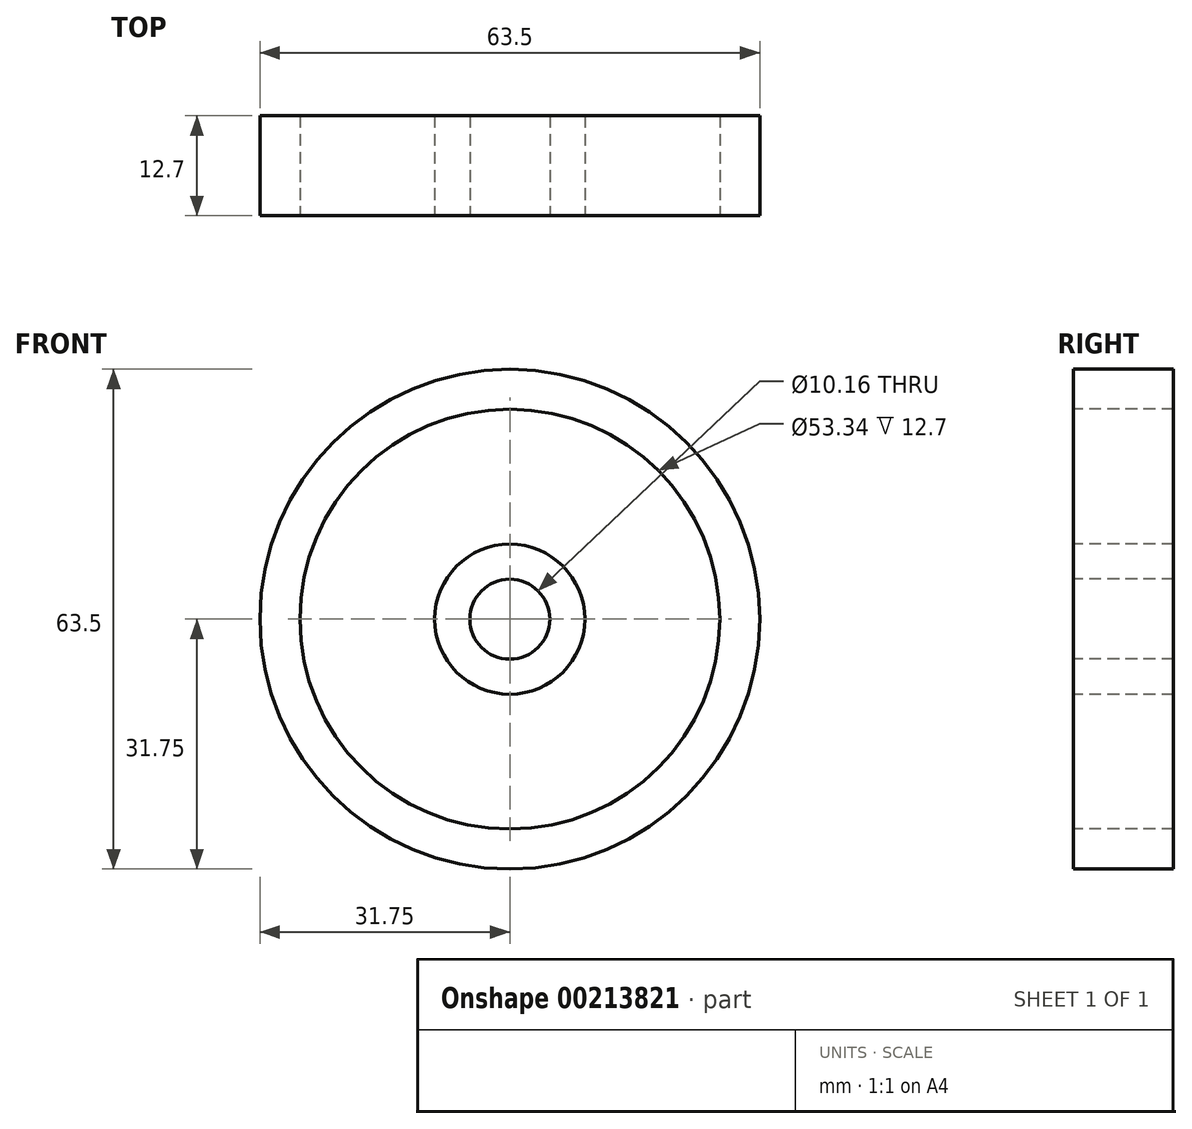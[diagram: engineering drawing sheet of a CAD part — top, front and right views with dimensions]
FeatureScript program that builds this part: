
annotation { "Feature Type Name" : "Feature", "Feature Type Description" : "" }
export const myFeature = defineFeature(function(context is Context, id is Id, definition is map)
    precondition{}
    {
        {
            var Q0;
            Q0=qCreatedBy(makeId("Front.planeOp"),FACE);
            var sketch = newSketch(context, id + "F0", { "sketchPlane" : qUnion([Q0])});
            skCircle(sketch, "E0", {"center": v(0, 0) * mm, "radius": 31.75 * mm});
            skSolve(sketch);
        }
        {
            var Q0;
            Q0=makeQuery(id+"F0.imprint","IMPRINT",FACE,{"disambiguationData":[TD([[makeQuery(id+"F0.imprint","IMPRINT",EDGE,{"derivedFrom":sQuery(id+"F0.wireOp",EDGE,"E0")}),1.0]])]});
            extrude(context, id + "F1", {"entities" : qUnion([Q0]), "depth" : 12.7 * mm});
        }
        {
            var Q0;
            Q0=makeQuery(id+"F1.opExtrude","CAP_FACE",FACE,{"disambiguationData":[OSD([sQuery(id+"F0.wireOp",EDGE,"E0")])],"isStart":false});
            var sketch = newSketch(context, id + "F2", { "sketchPlane" : qUnion([Q0])});
            skCircle(sketch, "E1", {"center": v(0, 0) * mm, "radius": 9.53 * mm});
            skSolve(sketch);
        }
        {
            var Q0;
            Q0=makeQuery(id+"F2.imprint","IMPRINT",FACE,{"disambiguationData":[TD([[makeQuery(id+"F2.imprint","IMPRINT",EDGE,{"derivedFrom":sQuery(id+"F2.wireOp",EDGE,"E1")}),-1.0]])]});
            var sketch = newSketch(context, id + "F3", { "sketchPlane" : qUnion([Q0])});
            skCircle(sketch, "E2", {"center": v(0, 0) * mm, "radius": 26.67 * mm});
            skSolve(sketch);
        }
        {
            var Q0;
            Q0 = qSketchRegion(id + "F3", true);
            extrude(context, id + "F4", {"entities" : qUnion([Q0]), "operationType" : NewBodyOperationType.REMOVE, "oppositeDirection" : true, "depth" : 25.4 * mm});
        }
        {
            var Q0;
            Q0=makeQuery(id+"F2.imprint","IMPRINT",FACE,{"disambiguationData":[TD([[makeQuery(id+"F2.imprint","IMPRINT",EDGE,{"derivedFrom":sQuery(id+"F2.wireOp",EDGE,"E1")}),1.0]])]});
            extrude(context, id + "F5", {"entities" : qUnion([Q0]), "oppositeDirection" : true, "depth" : 12.7 * mm});
        }
        {
            var Q0;
            Q0=makeQuery(id+"F1.opExtrude","CAP_FACE",FACE,{"disambiguationData":[OSD([sQuery(id+"F0.wireOp",EDGE,"E0")])],"isStart":false});
            var sketch = newSketch(context, id + "F6", { "sketchPlane" : qUnion([Q0])});
            skLineSegment(sketch, "E3", {"start": v(-16.38, 21.05) * mm, "end": v(12.6, -23.5) * mm});
            skLineSegment(sketch, "E4", {"start": v(-12.3, 23.67) * mm, "end": v(16.22, -21.17) * mm});
            skArc(sketch, "E5", {"start": v(-12.3, 23.67) * mm, "mid": v(-14.44, 22.52) * mm, "end": v(-16.38, 21.05) * mm});
            skArc(sketch, "E6", {"start": v(12.6, -23.5) * mm, "mid": v(14.57, -22.58) * mm, "end": v(16.22, -21.17) * mm});
            skSolve(sketch);
        }
        {
            var Q0;
            {var subQ0=sQuery(id+"F6.wireOp",EDGE,"E3");Q0=makeQuery(id+"F6.imprint","IMPRINT",FACE,{"disambiguationData":[TD([[makeQuery(id+"F6.imprint","IMPRINT",EDGE,{"derivedFrom":subQ0}),1.0]])]});}
            extrude(context, id + "F7", {"entities" : qUnion([Q0]), "operationType" : NewBodyOperationType.ADD, "oppositeDirection" : true, "depth" : 12.7 * mm});
        }
        {
            var Q0;
            Q0=makeQuery(id+"F1.opExtrude","CAP_FACE",FACE,{"disambiguationData":[OSD([sQuery(id+"F0.wireOp",EDGE,"E0")])],"isStart":false});
            var sketch = newSketch(context, id + "F8", { "sketchPlane" : qUnion([Q0])});
            skLineSegment(sketch, "E7", {"start": v(26.62, 17.3) * mm, "end": v(-19.29, -18.42) * mm});
            skLineSegment(sketch, "E8", {"start": v(23.93, 20.87) * mm, "end": v(-22.1, -14.94) * mm});
            skArc(sketch, "E9", {"start": v(22.6, 14.17) * mm, "mid": v(21.46, 16.11) * mm, "end": v(19.91, 17.74) * mm});
            skArc(sketch, "E10", {"start": v(-22.1, -14.94) * mm, "mid": v(-20.91, -16.86) * mm, "end": v(-19.29, -18.42) * mm});
            skSolve(sketch);
        }
        {
            var Q0;
            {var subQ0=sQuery(id+"F8.wireOp",EDGE,"E10");var subQ1=sQuery(id+"F8.wireOp",EDGE,"E7");var subQ2=makeQuery(id+"F4.boolean.opBoolean","COPY",EDGE,{"derivedFrom":makeQuery(id+"F4.opExtrude","CAP_EDGE",EDGE,{"disambiguationData":[OSD([sQuery(id+"F3.wireOp",EDGE,"E2")])],"isStart":true})});var subQ3=makeQuery(id+"F8.imprint","INTERSECT",VERTEX,{"derivedFrom":[subQ2,subQ1,subQ0]});Q0=makeQuery(id+"F8.imprint","IMPRINT",FACE,{"disambiguationData":[TD([[makeQuery(id+"F8.imprint","IMPRINT",EDGE,{"disambiguationData":[TD([[subQ3,1.0]])],"derivedFrom":subQ1}),-1.0]])]});}
            extrude(context, id + "F9", {"entities" : qUnion([Q0]), "operationType" : NewBodyOperationType.ADD, "oppositeDirection" : true, "depth" : 12.7 * mm});
        }
        {
            var Q0;
            {var subQ0=sQuery(id+"F3.wireOp",EDGE,"E2");Q0=makeQuery(id+"F9.boolean.opBoolean","MERGE",FACE,{"derivedFrom":[makeQuery(id+"F7.boolean.opBoolean","MERGE",FACE,{"derivedFrom":[makeQuery(id+"F5.opExtrude","CAP_FACE",FACE,{"disambiguationData":[OSD([sQuery(id+"F2.wireOp",EDGE,"E1")])],"isStart":true}),makeQuery(id+"F7.opExtrude","CAP_FACE",FACE,{"disambiguationData":[OSD([subQ0,sQuery(id+"F6.wireOp",EDGE,"E3"),sQuery(id+"F6.wireOp",EDGE,"E4")])],"isStart":true})]}),makeQuery(id+"F9.opExtrude","CAP_FACE",FACE,{"disambiguationData":[OSD([subQ0,sQuery(id+"F8.wireOp",EDGE,"E7"),sQuery(id+"F8.wireOp",EDGE,"E8")])],"isStart":true})]});}
            var sketch = newSketch(context, id + "F10", { "sketchPlane" : qUnion([Q0])});
            skCircle(sketch, "E11", {"center": v(0, 0) * mm, "radius": 5.08 * mm});
            skSolve(sketch);
        }
        {
            var Q0;
            Q0 = qSketchRegion(id + "F10", true);
            extrude(context, id + "F11", {"entities" : qUnion([Q0]), "operationType" : NewBodyOperationType.REMOVE, "oppositeDirection" : true, "depth" : 25.4 * mm});
        }
        {
            var Q0;
            Q0=makeQuery(id+"F1.opExtrude","CAP_FACE",FACE,{"disambiguationData":[OSD([sQuery(id+"F0.wireOp",EDGE,"E0")])],"isStart":false});
            shell(context, id + "F12", {"entities" : qUnion([Q0]), "thickness" : 2.54 * mm});
        }
        {
            var Q0;
            {var subQ0=sQuery(id+"F3.wireOp",EDGE,"E2");Q0=makeQuery(id+"F9.boolean.opBoolean","MERGE",FACE,{"derivedFrom":[makeQuery(id+"F7.boolean.opBoolean","MERGE",FACE,{"derivedFrom":[makeQuery(id+"F5.opExtrude","CAP_FACE",FACE,{"disambiguationData":[OSD([sQuery(id+"F2.wireOp",EDGE,"E1")])],"isStart":true}),makeQuery(id+"F7.opExtrude","CAP_FACE",FACE,{"disambiguationData":[OSD([subQ0,sQuery(id+"F6.wireOp",EDGE,"E3"),sQuery(id+"F6.wireOp",EDGE,"E4")])],"isStart":true})]}),makeQuery(id+"F9.opExtrude","CAP_FACE",FACE,{"disambiguationData":[OSD([subQ0,sQuery(id+"F8.wireOp",EDGE,"E7"),sQuery(id+"F8.wireOp",EDGE,"E8")])],"isStart":true})]});}
            var sketch = newSketch(context, id + "F13", { "sketchPlane" : qUnion([Q0])});
            skCircle(sketch, "E12", {"center": v(-9.29, 14.75) * mm, "radius": 1.1 * mm});
            skPoint(sketch, "E13.center.orphan", {"position": v(-6.94, 10.8) * mm});
            skSolve(sketch);
        }
        {
            var Q0;
            Q0 = qSketchRegion(id + "F13", true);
            extrude(context, id + "F14", {"entities" : qUnion([Q0]), "operationType" : NewBodyOperationType.REMOVE, "oppositeDirection" : true, "depth" : 25.4 * mm});
        }
        {
            var Q0;
            {var subQ0=sQuery(id+"F3.wireOp",EDGE,"E2");Q0=makeQuery(id+"F9.boolean.opBoolean","MERGE",FACE,{"derivedFrom":[makeQuery(id+"F7.boolean.opBoolean","MERGE",FACE,{"derivedFrom":[makeQuery(id+"F5.opExtrude","CAP_FACE",FACE,{"disambiguationData":[OSD([sQuery(id+"F2.wireOp",EDGE,"E1")])],"isStart":true}),makeQuery(id+"F7.opExtrude","CAP_FACE",FACE,{"disambiguationData":[OSD([subQ0,sQuery(id+"F6.wireOp",EDGE,"E3"),sQuery(id+"F6.wireOp",EDGE,"E4")])],"isStart":true})]}),makeQuery(id+"F9.opExtrude","CAP_FACE",FACE,{"disambiguationData":[OSD([subQ0,sQuery(id+"F8.wireOp",EDGE,"E7"),sQuery(id+"F8.wireOp",EDGE,"E8")])],"isStart":true})]});}
            var sketch = newSketch(context, id + "F15", { "sketchPlane" : qUnion([Q0])});
            skCircle(sketch, "E14", {"center": v(10.05, -15.37) * mm, "radius": 1.24 * mm});
            skSolve(sketch);
        }
        {
            var Q0;
            Q0 = qSketchRegion(id + "F15", true);
            extrude(context, id + "F16", {"entities" : qUnion([Q0]), "operationType" : NewBodyOperationType.REMOVE, "oppositeDirection" : true, "depth" : 25.4 * mm});
        }
        {
            var Q0;
            {var subQ0=sQuery(id+"F3.wireOp",EDGE,"E2");Q0=makeQuery(id+"F9.boolean.opBoolean","MERGE",FACE,{"derivedFrom":[makeQuery(id+"F7.boolean.opBoolean","MERGE",FACE,{"derivedFrom":[makeQuery(id+"F5.opExtrude","CAP_FACE",FACE,{"disambiguationData":[OSD([sQuery(id+"F2.wireOp",EDGE,"E1")])],"isStart":true}),makeQuery(id+"F7.opExtrude","CAP_FACE",FACE,{"disambiguationData":[OSD([subQ0,sQuery(id+"F6.wireOp",EDGE,"E3"),sQuery(id+"F6.wireOp",EDGE,"E4")])],"isStart":true})]}),makeQuery(id+"F9.opExtrude","CAP_FACE",FACE,{"disambiguationData":[OSD([subQ0,sQuery(id+"F8.wireOp",EDGE,"E7"),sQuery(id+"F8.wireOp",EDGE,"E8")])],"isStart":true})]});}
            var sketch = newSketch(context, id + "F17", { "sketchPlane" : qUnion([Q0])});
            skCircle(sketch, "E15", {"center": v(-14.04, -11.22) * mm, "radius": 1.18 * mm});
            skCircle(sketch, "E16", {"center": v(14.94, 11.32) * mm, "radius": 1.1 * mm});
            skSolve(sketch);
        }
        {
            var Q0;
            Q0 = qSketchRegion(id + "F17", true);
            extrude(context, id + "F18", {"entities" : qUnion([Q0]), "operationType" : NewBodyOperationType.REMOVE, "oppositeDirection" : true, "depth" : 25.4 * mm});
        }
    });
